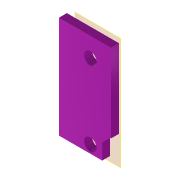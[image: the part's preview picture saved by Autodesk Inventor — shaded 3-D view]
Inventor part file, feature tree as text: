
AUTODESK INVENTOR PART (.ipt)
format: ipt  version: 2022 (Build 260153000, 153)  size: 120,320 bytes
history: native  units: mm
features: extrude x2, sketch x2, reference x2, other x2, plane x1, projected_geometry x1
ambient origin geometry x8: Origin, YZ Plane, XZ Plane, XY Plane, X Axis, Y Axis, Z Axis, Center Point
bodies: Volumenkörper1 (feature_tree)
feature tree (10):
  plane  "Arbeitsebene1"
  extrude  "Extrusion1"  Depth=3.3mm
  extrude  "Extrusion2"  Depth=10.0mm TaperAngle=0.0deg
  sketch  "Skizze1"  dims[d0=3.3mm d1=3.3mm]
  reference  "Referenz1"
  sketch  "Skizze2"  dims[d2=2.0mm d3=0.0mm d4=10.0mm d5=0.0mm]
  reference  "Referenz2"
  projected_geometry  "Projizierte Kontur1"
  other  "Camera_Autofocus_Mount.iam"
  other  "Baugruppe1"
